# Revit family: Maxlogic Détecteur de beam linéaire
name_source: partatom
category: Fire Alarm Devices
units: mm (PartAtom-declared; Revit-internal decimal feet)

## family parameters
Cut with Voids When Loaded = No
Host = Face
Maintain Annotation Orientation = Yes
OmniClass Number = 23.85.30.21
OmniClass Title = Environmental Detection/Registration
Part Type = Normal
Room Calculation Point = No
Round Connector Dimension = Use Diameter
Shared = No

## types (6) — shared parameters
Adresse ligne 1 = Şerifali Mahallesi Kutup Sokak No:27/1-2-4 Ümraniye TR-34775 İSTANBUL
Alimentation d'externe = 24 V/DC
Code de  Performance = EN 54-12 ve EN 54-17
Couleur = Blanc
Deuxime Matèriel = Plastique
Durée de la garantie Travail = 2
Durée de la garantie réservé = 2
Hauteur Nominale = 160 mm
Hauteur de Montage = Il faut l'installer %10 du hauteur plafond
Largeur Nominale = 109 mm
Longeur Nominale = 192 mm
Manuel d'installation = https://mavilielektronik.com
Manufacturer = Mavili Elektronik Ticaret A.Ş.
Model = MaxLogic
Numèro de Fax = (+)90 216 466 45 10
Poids = 830 gr.
Surface de Montage = Montage à Mur
Tempèrature de Fonctionnement = (-10°C) - (+55°C)
URL = https://www.mavili.com.tr
Unité de durée de garantie = Ans
Voltage de fonctionnement (default) = 20V - 30V DC
zero-valued in all types: Cost, Default Elevation

## per-type parameters (varying)
| type | Charger adresse d'appareil | Code de Produit | Description | Matériel Principe | Numéro de pose des travaux publics | Réflecteur |
| Maxlogic détecteur de fumée lineaire adressable | Appareil d'adressage à main | ML-1170 | Détecteur de fumée lineaire adressable | Plastique Blanche PC/ABS |  |  |
| Maxlogic Détecteur de fumée linaire adressable , Isolateur de Court-Circuit | Appareil d'adresage à Main | ML-1170.SCI | Détecteur de fumée linaire adressable , Isolateur de Court-Circuit | Plastique Blanche  PC/ABS |  |  |
| Maxlogic détecteur de fumée lineaire adressable avec reflecteur | Appareil d'adressage à Main | ML-1173 | Détecteur de fumée lineaire adressable | Plastique Blanc PC/ABS |  | ML-0171 ve ML-0174 |
| Maxlogic détecteur de fumée lineaire adressable avec reflecteur ,Isolateur de Court-Circuit | Appareil d'adressage à Main | ML-1173.SCI | détecteur de fumée lineaire adressable avec reflecteur ,Isolateur de Court-Circuit | Plastique Blanche PC/ABS |  | ML-0171 ve ML-0174 |
| Maxlogic détecteur de fumée lineaire  conventionnelle |  | ML-2170 | Détecteur de fumée lineaire  conventionnelle | Plastique Blanche PC/ABS | 832-111 |  |
| Maxlogic Détecteur de fumée lineaire conventionnelle avec reflecteur |  | ML-2173 | Détecteur de fumée lineaire  conventionnelle avec reflecteur | Plastique Blanche PC/ABS |  | ML-0171 ve ML-0174 |

## geometry (parser evidence)
native form markers: Sweep x2
no freeform markers — native parametric forms only
